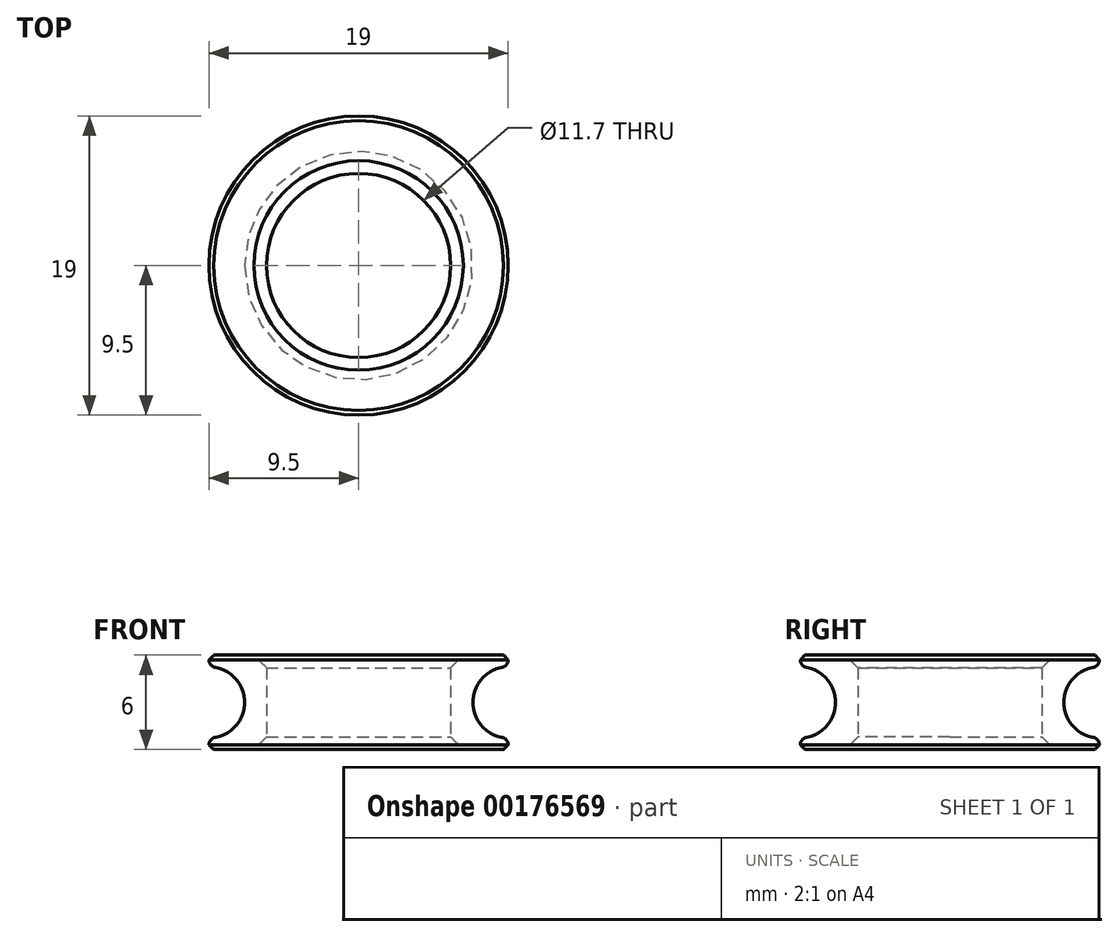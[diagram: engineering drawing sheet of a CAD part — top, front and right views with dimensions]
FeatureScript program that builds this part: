
annotation { "Feature Type Name" : "Feature", "Feature Type Description" : "" }
export const myFeature = defineFeature(function(context is Context, id is Id, definition is map)
    precondition{}
    {
        {
            var Q0;
            Q0=qCreatedBy(makeId("Front.planeOp"),FACE);
            var sketch = newSketch(context, id + "F0", { "sketchPlane" : qUnion([Q0])});
            skLineSegment(sketch, "E0", {"start": v(0, 0) * mm, "end": v(0, 44.74) * mm, "construction": true});
            skLineSegment(sketch, "E1", {"start": v(5.85, 0) * mm, "end": v(5.85, 6) * mm});
            skLineSegment(sketch, "E2", {"start": v(5.85, 6) * mm, "end": v(9.5, 6) * mm});
            skLineSegment(sketch, "E3", {"start": v(9.5, 6) * mm, "end": v(9.5, 5.7) * mm});
            skLineSegment(sketch, "E4", {"start": v(9.5, 0.3) * mm, "end": v(9.5, 0) * mm});
            skLineSegment(sketch, "E5", {"start": v(9.5, 0) * mm, "end": v(5.85, 0) * mm});
            skArc(sketch, "E6", {"start": v(9.1, 5.21) * mm, "mid": v(7.25, 3) * mm, "end": v(9.1, 0.79) * mm});
            skLineSegment(sketch, "E7", {"start": v(9.5, 5.25) * mm, "end": v(9.5, 0.75) * mm, "construction": true});
            skPoint(sketch, "E8.visualSharp", {"position": v(9.5, 0.75) * mm});
            skArc(sketch, "E8.filletArc", {"start": v(9.5, 0.3) * mm, "mid": v(9.38, 0.61) * mm, "end": v(9.1, 0.79) * mm});
            skPoint(sketch, "E9.visualSharp", {"position": v(9.5, 5.25) * mm});
            skArc(sketch, "E9.filletArc", {"start": v(9.1, 5.21) * mm, "mid": v(9.38, 5.39) * mm, "end": v(9.5, 5.7) * mm});
            skSolve(sketch);
        }
        {
            var Q0;
            Q0=makeQuery(id+"F0.imprint","IMPRINT",FACE,{"disambiguationData":[TD([[makeQuery(id+"F0.imprint","IMPRINT",EDGE,{"derivedFrom":sQuery(id+"F0.wireOp",EDGE,"E1")}),-1.0]])]});
            var Q1;
            Q1=sQuery(id+"F0.wireOp",EDGE,"E0");
            revolve(context, id + "F1", {"entities" : qUnion([Q0]), "axis" : qUnion([Q1]), "revolveType" : RevolveType.FULL});
        }
        {
            var Q0;
            Q0=makeQuery(id+"F1.opRevolve","SWEPT_EDGE",EDGE,{"disambiguationData":[OSD([sQuery(id+"F0.wireOp",EDGE,"E1"),sQuery(id+"F0.wireOp",EDGE,"E5")])]});
            var Q1;
            Q1=makeQuery(id+"F1.opRevolve","SWEPT_EDGE",EDGE,{"disambiguationData":[OSD([sQuery(id+"F0.wireOp",EDGE,"E1"),sQuery(id+"F0.wireOp",EDGE,"E2")])]});
            chamfer(context, id + "F2", {"entities" : qUnion([Q0, Q1]), "width" : 0.8 * mm, "tangentPropagation" : true});
        }
        {
            var Q0;
            Q0=makeQuery(id+"F1.opRevolve","SWEPT_EDGE",EDGE,{"disambiguationData":[OSD([sQuery(id+"F0.wireOp",EDGE,"E2"),sQuery(id+"F0.wireOp",EDGE,"E3")])]});
            var Q1;
            Q1=makeQuery(id+"F1.opRevolve","SWEPT_EDGE",EDGE,{"disambiguationData":[OSD([sQuery(id+"F0.wireOp",EDGE,"E4"),sQuery(id+"F0.wireOp",EDGE,"E5")])]});
            chamfer(context, id + "F3", {"entities" : qUnion([Q0, Q1]), "width" : 0.3 * mm, "tangentPropagation" : true});
        }
    });
